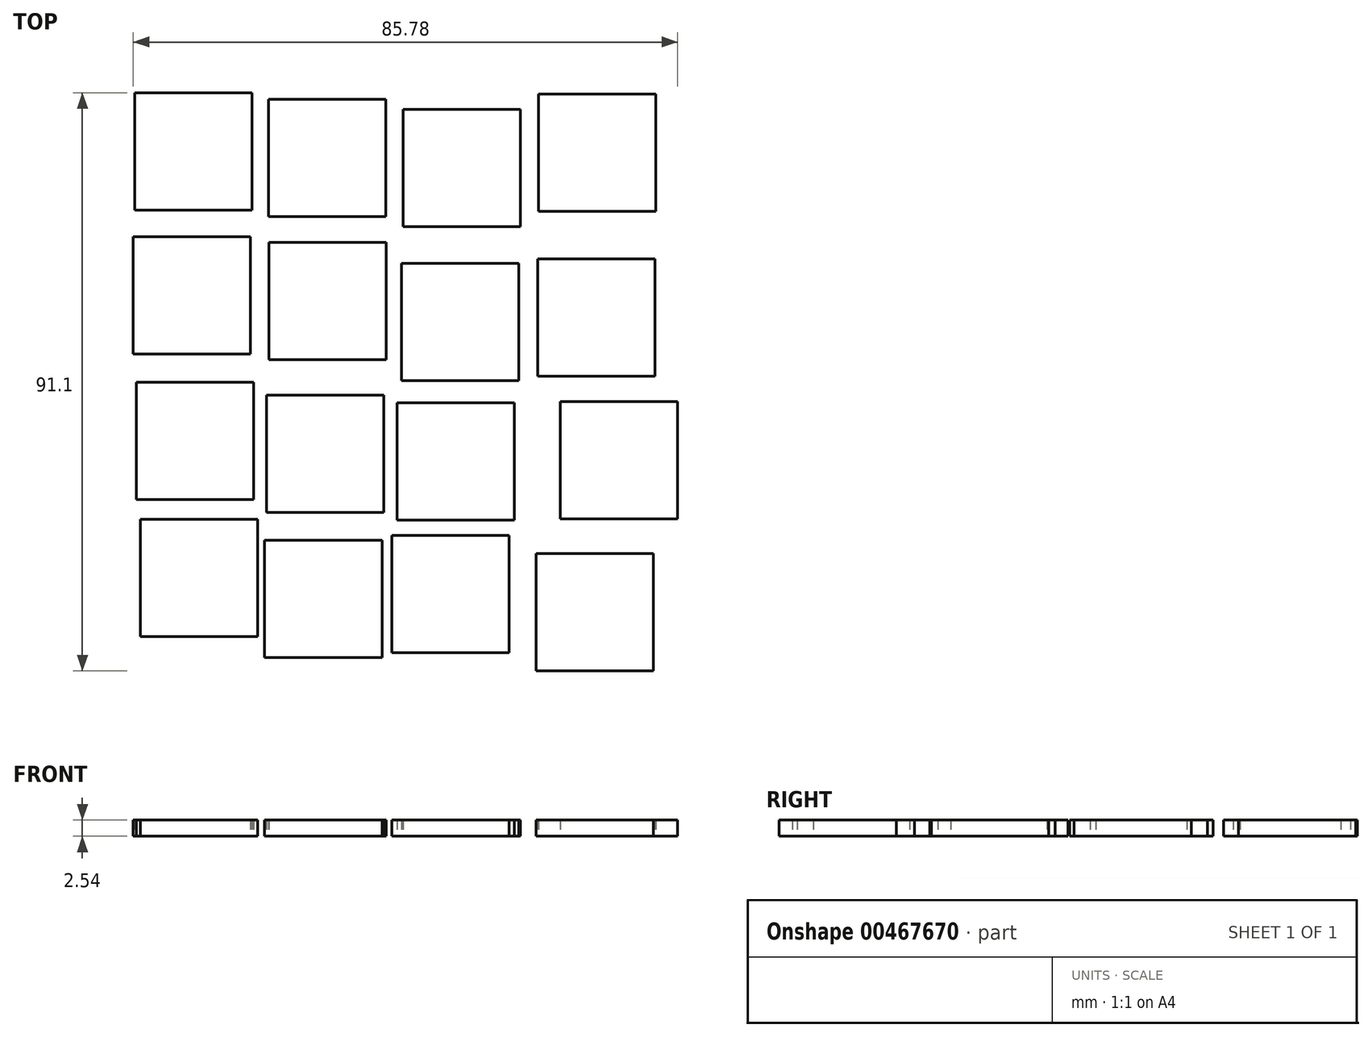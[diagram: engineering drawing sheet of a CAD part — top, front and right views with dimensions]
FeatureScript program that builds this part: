
annotation { "Feature Type Name" : "Feature", "Feature Type Description" : "" }
export const myFeature = defineFeature(function(context is Context, id is Id, definition is map)
    precondition{}
    {
        {
            var Q0;
            Q0=qCreatedBy(makeId("Top.planeOp"),FACE);
            var sketch = newSketch(context, id + "F0", { "sketchPlane" : qUnion([Q0])});
            skLineSegment(sketch, "E0.bottom", {"start": v(-47.5, 58.72) * mm, "end": v(-29.02, 58.72) * mm});
            skLineSegment(sketch, "E0.top", {"start": v(-47.5, 40.24) * mm, "end": v(-29.02, 40.24) * mm});
            skLineSegment(sketch, "E0.left", {"start": v(-47.5, 58.72) * mm, "end": v(-47.5, 40.24) * mm});
            skLineSegment(sketch, "E0.right", {"start": v(-29.02, 58.72) * mm, "end": v(-29.02, 40.24) * mm});
            skLineSegment(sketch, "E1.bottom", {"start": v(-26.53, 32.9) * mm, "end": v(-8.04, 32.9) * mm});
            skLineSegment(sketch, "E1.top", {"start": v(-26.53, 14.42) * mm, "end": v(-8.04, 14.42) * mm});
            skLineSegment(sketch, "E1.left", {"start": v(-26.53, 32.9) * mm, "end": v(-26.53, 14.42) * mm});
            skLineSegment(sketch, "E1.right", {"start": v(-8.04, 32.9) * mm, "end": v(-8.04, 14.42) * mm});
            skLineSegment(sketch, "E2.bottom", {"start": v(-1.52, 11.11) * mm, "end": v(16.96, 11.11) * mm});
            skLineSegment(sketch, "E2.top", {"start": v(-1.52, -7.37) * mm, "end": v(16.96, -7.37) * mm});
            skLineSegment(sketch, "E2.left", {"start": v(-1.52, 11.11) * mm, "end": v(-1.52, -7.37) * mm});
            skLineSegment(sketch, "E2.right", {"start": v(16.96, 11.11) * mm, "end": v(16.96, -7.37) * mm});
            skLineSegment(sketch, "E3.bottom", {"start": v(-47.8, 12.13) * mm, "end": v(-29.32, 12.13) * mm});
            skLineSegment(sketch, "E3.top", {"start": v(-47.8, -6.35) * mm, "end": v(-29.32, -6.35) * mm});
            skLineSegment(sketch, "E3.left", {"start": v(-47.8, 12.13) * mm, "end": v(-47.8, -6.35) * mm});
            skLineSegment(sketch, "E3.right", {"start": v(-29.32, 12.13) * mm, "end": v(-29.32, -6.35) * mm});
            skLineSegment(sketch, "E4.bottom", {"start": v(-68.82, 37.04) * mm, "end": v(-50.34, 37.04) * mm});
            skLineSegment(sketch, "E4.top", {"start": v(-68.82, 18.56) * mm, "end": v(-50.34, 18.56) * mm});
            skLineSegment(sketch, "E4.left", {"start": v(-68.82, 37.04) * mm, "end": v(-68.82, 18.56) * mm});
            skLineSegment(sketch, "E4.right", {"start": v(-50.34, 37.04) * mm, "end": v(-50.34, 18.56) * mm});
            skLineSegment(sketch, "E5.bottom", {"start": v(-4.99, 59.52) * mm, "end": v(13.5, 59.52) * mm});
            skLineSegment(sketch, "E5.top", {"start": v(-4.99, 41.04) * mm, "end": v(13.5, 41.04) * mm});
            skLineSegment(sketch, "E5.left", {"start": v(-4.99, 59.52) * mm, "end": v(-4.99, 41.04) * mm});
            skLineSegment(sketch, "E5.right", {"start": v(13.5, 59.52) * mm, "end": v(13.5, 41.04) * mm});
            skLineSegment(sketch, "E6.bottom", {"start": v(-28.1, -10) * mm, "end": v(-9.61, -10) * mm});
            skLineSegment(sketch, "E6.top", {"start": v(-28.1, -28.47) * mm, "end": v(-9.61, -28.47) * mm});
            skLineSegment(sketch, "E6.left", {"start": v(-28.1, -10) * mm, "end": v(-28.1, -28.47) * mm});
            skLineSegment(sketch, "E6.right", {"start": v(-9.61, -10) * mm, "end": v(-9.61, -28.47) * mm});
            skLineSegment(sketch, "E7.bottom", {"start": v(-67.7, -7.45) * mm, "end": v(-49.21, -7.45) * mm});
            skLineSegment(sketch, "E7.top", {"start": v(-67.7, -25.93) * mm, "end": v(-49.21, -25.93) * mm});
            skLineSegment(sketch, "E7.left", {"start": v(-67.7, -7.45) * mm, "end": v(-67.7, -25.93) * mm});
            skLineSegment(sketch, "E7.right", {"start": v(-49.21, -7.45) * mm, "end": v(-49.21, -25.93) * mm});
            skLineSegment(sketch, "E8.bottom", {"start": v(-68.61, 59.76) * mm, "end": v(-50.13, 59.76) * mm});
            skLineSegment(sketch, "E8.top", {"start": v(-68.61, 41.27) * mm, "end": v(-50.13, 41.27) * mm});
            skLineSegment(sketch, "E8.left", {"start": v(-68.61, 59.76) * mm, "end": v(-68.61, 41.27) * mm});
            skLineSegment(sketch, "E8.right", {"start": v(-50.13, 59.76) * mm, "end": v(-50.13, 41.27) * mm});
            skLineSegment(sketch, "E9.bottom", {"start": v(-68.3, 14.16) * mm, "end": v(-49.82, 14.16) * mm});
            skLineSegment(sketch, "E9.top", {"start": v(-68.3, -4.32) * mm, "end": v(-49.82, -4.32) * mm});
            skLineSegment(sketch, "E9.left", {"start": v(-68.3, 14.16) * mm, "end": v(-68.3, -4.32) * mm});
            skLineSegment(sketch, "E9.right", {"start": v(-49.82, 14.16) * mm, "end": v(-49.82, -4.32) * mm});
            skLineSegment(sketch, "E10.bottom", {"start": v(-48.1, -10.75) * mm, "end": v(-29.63, -10.75) * mm});
            skLineSegment(sketch, "E10.top", {"start": v(-48.1, -29.23) * mm, "end": v(-29.63, -29.23) * mm});
            skLineSegment(sketch, "E10.left", {"start": v(-48.1, -10.75) * mm, "end": v(-48.1, -29.23) * mm});
            skLineSegment(sketch, "E10.right", {"start": v(-29.63, -10.75) * mm, "end": v(-29.63, -29.23) * mm});
            skLineSegment(sketch, "E11.bottom", {"start": v(-47.45, 36.17) * mm, "end": v(-28.97, 36.17) * mm});
            skLineSegment(sketch, "E11.top", {"start": v(-47.45, 17.69) * mm, "end": v(-28.97, 17.69) * mm});
            skLineSegment(sketch, "E11.left", {"start": v(-47.45, 36.17) * mm, "end": v(-47.45, 17.69) * mm});
            skLineSegment(sketch, "E11.right", {"start": v(-28.97, 36.17) * mm, "end": v(-28.97, 17.69) * mm});
            skLineSegment(sketch, "E12.bottom", {"start": v(-26.3, 57.16) * mm, "end": v(-7.82, 57.16) * mm});
            skLineSegment(sketch, "E12.top", {"start": v(-26.3, 38.68) * mm, "end": v(-7.82, 38.68) * mm});
            skLineSegment(sketch, "E12.left", {"start": v(-26.3, 57.16) * mm, "end": v(-26.3, 38.68) * mm});
            skLineSegment(sketch, "E12.right", {"start": v(-7.82, 57.16) * mm, "end": v(-7.82, 38.68) * mm});
            skLineSegment(sketch, "E13.bottom", {"start": v(-27.26, 10.9) * mm, "end": v(-8.78, 10.9) * mm});
            skLineSegment(sketch, "E13.top", {"start": v(-27.26, -7.58) * mm, "end": v(-8.78, -7.58) * mm});
            skLineSegment(sketch, "E13.left", {"start": v(-27.26, 10.9) * mm, "end": v(-27.26, -7.58) * mm});
            skLineSegment(sketch, "E13.right", {"start": v(-8.78, 10.9) * mm, "end": v(-8.78, -7.58) * mm});
            skLineSegment(sketch, "E14.bottom", {"start": v(-5.31, -12.86) * mm, "end": v(13.17, -12.86) * mm});
            skLineSegment(sketch, "E14.top", {"start": v(-5.31, -31.34) * mm, "end": v(13.17, -31.34) * mm});
            skLineSegment(sketch, "E14.left", {"start": v(-5.31, -12.86) * mm, "end": v(-5.31, -31.34) * mm});
            skLineSegment(sketch, "E14.right", {"start": v(13.17, -12.86) * mm, "end": v(13.17, -31.34) * mm});
            skLineSegment(sketch, "E15.bottom", {"start": v(-5.1, 33.59) * mm, "end": v(13.39, 33.59) * mm});
            skLineSegment(sketch, "E15.top", {"start": v(-5.1, 15.1) * mm, "end": v(13.39, 15.1) * mm});
            skLineSegment(sketch, "E15.left", {"start": v(-5.1, 33.59) * mm, "end": v(-5.1, 15.1) * mm});
            skLineSegment(sketch, "E15.right", {"start": v(13.39, 33.59) * mm, "end": v(13.39, 15.1) * mm});
            skSolve(sketch);
        }
        {
            var Q0;
            Q0 = qSketchRegion(id + "F0", true);
            extrude(context, id + "F1", {"entities" : qUnion([Q0]), "depth" : 2.54 * mm});
        }
    });
